# Revit family: KDW010091
name_source: partatom
category: Plumbing Fixtures
revit_build: Autodesk Revit 2015 (Build: 20140606_1530(x64)
units: mm (PartAtom-declared; Revit-internal decimal feet)

## types (1)
- CONO EINBAUWASCHTISCH 3082 500x1200
    BIMobject category = Basins
    Brand url = http://www.kaldewei.com
    Color = https://www.kaldewei.co.uk
    ColourOptions = https://www.kaldewei.co.uk
    Design country = Germany
    Durability = https://www.kaldewei.de
    Edition number = 1
    Features = https://www.kaldewei.co.uk
    Finish = https://n
    Finition = Kaldewei
    HasGrabHandles = https://www.kaldewei.co.uk
    IFC Classification = Furnishing Element
    IfcExportAs = WASHHANDBASIN
    IfcExportType = IfcSanitaryTerminalType
    IntegralAccessories = https://www.kaldewei.co.uk
    Manufacturer = Kaldewei
    Manufacturer country = Germany
    ManufacturerCountry = GERMANY
    ManufacturerName = KALDEWEI
    ManufacturerURL = https://www.kaldewei.com
    Material = steel enamel
    Material main = Steel
    Material secondary = Enamel
    Metal = Chrome
    Model = CONO EINBAUWASCHTISCH
    NBS Reference Code = 35-65-70-94
    NBS Reference Description = Wash Basin Systems
    Name = CONO Built-in washbasin
    Nominal height = 1200 cm
    Nominal width = 500 cm
    NominalLength = 1200
    ObjectName = CONO Built-in washbasin 500x1200
    ObjectNorm = EN 14688EU DECLARATION OF PERFORMANCE(https://www.kaldewei.de
    ObjectPicture = https://www.kaldewei.co.uk
    ObjectURL = https://www.kaldewei.co.uk
    Polantis code = KDW010091
    Product Guid = e0df5077-030c-4800-9d43-58773ddcb561
    Product SKU = 3082
    Product certification = https://www.kaldewei.co.uk
    Product data url = https://bimobject.com
    Product family = CONO
    Product group = Washbasin
    Product url = https://www.kaldewei.co.uk
    ProductInformation = Model No.3082: - washbasin with premium character exudes elegance and harmony- optimally integrated enamelled waste accentuates the underlying geometry of the washbasin- unusually generous rim provides space for fittings or individual accessories- perfectly complements the Cono range- All CONO washbasins of 120 cm width are available now with 1x1 or 1x3 tap holes
    QR code = http://bimobject.com
    Revision = 1
    SerialNumber = 3082
    Shape = Built-In,Double washbasin
    Size = 500x1200
    SupportFrame = https://www.kaldewei.co.uk
    Sustainability = https://kaldewei-fa.secure.footprint.net
    Technical description = https://www.kaldewei.co.uk
    TechnicalDataURL = https://kaldewei.typo-live.web-factory.de
    Type Comments = CONO EINBAUWASCHTISCH 3082 500x1200
    UNSPSC Code = 301815
    UNSPSCCode = 30181504
    UNSPSCNames = Sinks
    URL = https://www.kaldewei.co.uk
    Uniclass 1.4 Code = L7212
    Uniclass 1.4 Description = Washbasins
    Uniclass 2.0 Code = SS-35-65-70-94
    Uniclass 2.0 Description = Wash Basin Systems
    Uniclass 2015 = Pr_40_20_96
    Version = 5
    WarrantyDurationParts = 30
    WarrantyDurationUnit = Year
    WarrantyStartDate = https://www.kaldewei.co.uk
    Weight = 15,9
    Weight Net (Kg) = 15.9

## geometry (parser evidence)
native form markers: Sweep x2
no freeform markers — native parametric forms only
